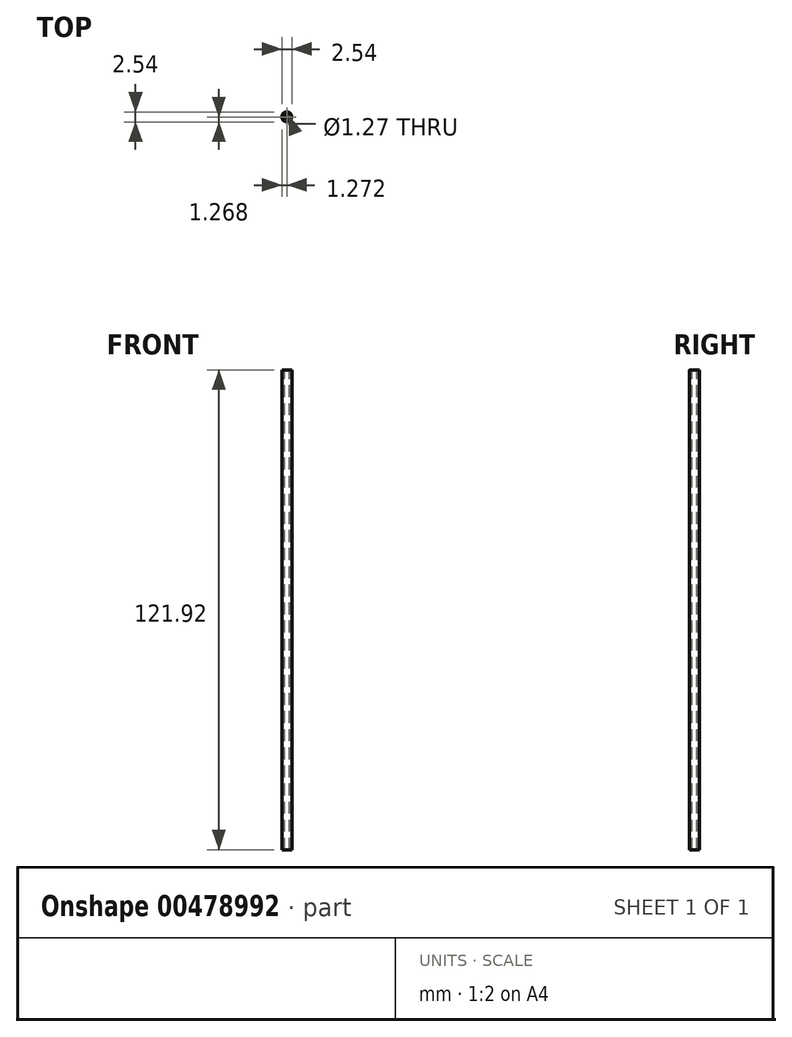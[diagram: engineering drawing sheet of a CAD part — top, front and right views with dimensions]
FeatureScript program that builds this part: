
annotation { "Feature Type Name" : "Feature", "Feature Type Description" : "" }
export const myFeature = defineFeature(function(context is Context, id is Id, definition is map)
    precondition{}
    {
        {
            var Q0;
            Q0=qCreatedBy(makeId("Top.planeOp"),FACE);
            var sketch = newSketch(context, id + "F0", { "sketchPlane" : qUnion([Q0])});
            skCircle(sketch, "E0", {"center": v(-33.1, 17.27) * mm, "radius": 1.27 * mm});
            skSolve(sketch);
        }
        {
            var Q0;
            Q0 = qSketchRegion(id + "F0", true);
            extrude(context, id + "F1", {"entities" : qUnion([Q0]), "depth" : 121.92 * mm});
        }
        {
            var Q0;
            Q0=makeQuery(id+"F1.opExtrude","CAP_FACE",FACE,{"disambiguationData":[OSD([sQuery(id+"F0.wireOp",EDGE,"E0")])],"isStart":false});
            var sketch = newSketch(context, id + "F2", { "sketchPlane" : qUnion([Q0])});
            skCircle(sketch, "E1", {"center": v(-33.1, 17.27) * mm, "radius": 0.64 * mm});
            skSolve(sketch);
        }
        {
            var Q0;
            Q0=makeQuery(id+"F2.imprint","IMPRINT",FACE,{"disambiguationData":[TD([[makeQuery(id+"F2.imprint","IMPRINT",EDGE,{"derivedFrom":sQuery(id+"F2.wireOp",EDGE,"E1")}),1.0]])]});
            extrude(context, id + "F3", {"entities" : qUnion([Q0]), "operationType" : NewBodyOperationType.REMOVE, "oppositeDirection" : true, "depth" : 121.92 * mm, "hasSecondDirection" : true, "secondDirectionOppositeDirection" : false, "secondDirectionDepth" : 25.4 * mm});
        }
    });
